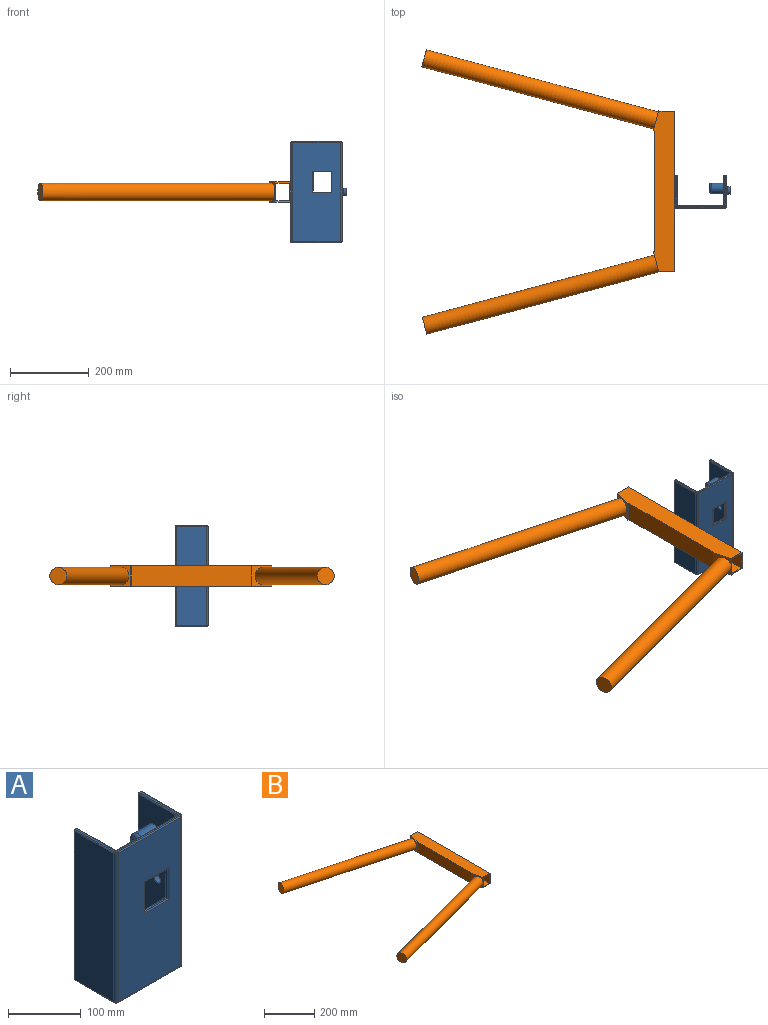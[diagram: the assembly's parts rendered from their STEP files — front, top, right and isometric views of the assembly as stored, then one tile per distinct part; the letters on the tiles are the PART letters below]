
ASSEMBLY  parts=2 mates=1
PART A: 63 faces, bbox 141.6x83.2x254.2 mm
  f0: cylinder r=5.08mm len=243.28mm, axis (0,0,-1), area 1941.3mm2, adj f1,f11,f12,f56
  f1: bspline ~5.34x5.34mm, area 34.1mm2, adj f0,f4,f11,f12,f37,f39
  f2: cylinder r=5.08mm len=243.28mm, axis (0,0,1), area 1941.3mm2, adj f3,f11,f17,f55
  f3: bspline ~5.34x5.34mm, area 34.1mm2, adj f2,f7,f11,f17,f34,f36
  f4: bspline ~5.77x5.77mm, area 13.8mm2, adj f1,f37,f39
  f5: bspline ~5.62x5.59mm, area 13.9mm2, adj f36,f38,f56
  f6: bspline ~5.77x5.77mm, area 13.8mm2, adj f35,f37,f55
  f7: bspline ~5.62x5.59mm, area 13.9mm2, adj f3,f34,f36
  f8: plane 128.27x80.96mm, normal (0,0,1), area 896mm2, adj f13,f16,f34,f36,f38,f42,f44,f46
  f9: plane 128.27x80.96mm, normal (0,0,-1), area 896mm2, adj f13,f16,f35,f37,f39,f43,f45,f47
  f10: plane 250.83x121.29mm, normal (0,-1,0), area 27782.2mm2, adj f29,f30,f31,f32,f44,f45,f50,f53
  f11: plane 251.07x108.83mm, normal (0,1,0), area 24682.4mm2, adj f0,f1,f2,f3,f25,f26,f27,f28
  f12: plane 251.07x69.78mm, normal (1,0,0), area 17440.5mm2, adj f0,f1,f38,f39,f40,f56
  f13: plane 254x3.18mm, normal (0,1,0), area 806.4mm2, adj f8,f9,f40,f48
  f14: plane 250.83x75.88mm, normal (-1,0,0), area 19033.2mm2, adj f46,f47,f48,f53
  f15: plane 250.83x75.88mm, normal (1,0,0), area 18526.5mm2, adj f41,f42,f43,f50,f62
  f16: plane 254x3.18mm, normal (0,1,0), area 806.4mm2, adj f8,f9,f33,f41
  f17: plane 251.07x69.78mm, normal (-1,0,0), area 16300.4mm2, adj f2,f3,f18,f20,f33,f34,f35,f55
  f18: cylinder r=12.7mm len=31.75mm, axis (1,0,0), area 2533.5mm2, adj f17,f58
  f19: plane 15.24x15.24mm, normal (-1,0,0), area 182.4mm2, adj f58
  f20: cylinder r=12.7mm len=31.75mm, axis (1,0,0), area 2533.5mm2, adj f17,f57
  f21: plane 15.24x15.24mm, normal (-1,0,0), area 182.4mm2, adj f57
  f22: plane 45.72x3.18mm, normal (0,0,-1), area 145.2mm2, adj f23,f25,f28,f29
  f23: plane 50.8x3.18mm, normal (1,0,0), area 161.3mm2, adj f22,f24,f27,f30
  f24: plane 45.72x3.18mm, normal (0,0,1), area 145.2mm2, adj f23,f25,f26,f32
  f25: plane 53.98x4.76mm, normal (-1,0,0), area 243mm2, adj f11,f22,f24,f26,f28,f31
  f26: cylinder r=1.59mm len=47.31mm, axis (1,0,0), area 116mm2, adj f11,f24,f25,f27
  f27: cylinder r=1.59mm len=53.98mm, axis (0,0,-1), area 130.6mm2, adj f11,f23,f26,f28
  f28: cylinder r=1.59mm len=47.31mm, axis (-1,0,0), area 116mm2, adj f11,f22,f25,f27
  f29: cylinder r=1.59mm len=48.9mm, axis (1,0,0), area 118mm2, adj f10,f22,f30,f31
  f30: cylinder r=1.59mm len=53.98mm, axis (0,0,1), area 130.6mm2, adj f10,f23,f29,f32
  f31: cylinder r=1.59mm len=53.98mm, axis (0,0,-1), area 130.6mm2, adj f10,f25,f29,f32
  f32: cylinder r=1.59mm len=48.9mm, axis (-1,0,0), area 118mm2, adj f10,f24,f30,f31
  f33: cylinder r=1.59mm len=254mm, axis (0,0,1), area 629.4mm2, adj f16,f17,f34,f35
  f34: cylinder r=1.59mm len=77.79mm, axis (0,1,0), area 182mm2, adj f3,f7,f8,f17,f33
  f35: cylinder r=1.59mm len=77.79mm, axis (0,-1,0), area 182mm2, adj f6,f9,f17,f33,f55
  f36: cylinder r=1.59mm len=121.92mm, axis (1,0,0), area 284mm2, adj f3,f5,f7,f8,f11,f56
  f37: cylinder r=1.59mm len=121.92mm, axis (-1,0,0), area 284mm2, adj f1,f4,f6,f9,f11,f55
  f38: cylinder r=1.59mm len=77.79mm, axis (0,-1,0), area 182mm2, adj f5,f8,f12,f40,f56
  f39: cylinder r=1.59mm len=77.79mm, axis (0,1,0), area 182mm2, adj f1,f4,f9,f12,f40
  f40: cylinder r=1.59mm len=254mm, axis (0,0,1), area 629.4mm2, adj f12,f13,f38,f39
  f41: cylinder r=1.59mm len=254mm, axis (0,0,-1), area 629.4mm2, adj f15,f16,f42,f43
  f42: cylinder r=1.59mm len=77.47mm, axis (0,-1,0), area 191.2mm2, adj f8,f15,f41,f49
  f43: cylinder r=1.59mm len=77.47mm, axis (0,1,0), area 191.2mm2, adj f9,f15,f41,f51
  f44: cylinder r=1.59mm len=121.29mm, axis (-1,0,0), area 302.4mm2, adj f8,f10,f49,f52
  f45: cylinder r=1.59mm len=121.29mm, axis (1,0,0), area 302.4mm2, adj f9,f10,f51,f54
  f46: cylinder r=1.59mm len=77.47mm, axis (0,1,0), area 191.2mm2, adj f8,f14,f48,f52
  f47: cylinder r=1.59mm len=77.47mm, axis (0,-1,0), area 191.2mm2, adj f9,f14,f48,f54
  f48: cylinder r=1.59mm len=254mm, axis (0,0,-1), area 629.4mm2, adj f13,f14,f46,f47
  f49: torus R=3.49mm, axis (0,0,1), area 17.6mm2, adj f8,f42,f44,f50
  f50: cylinder r=5.08mm len=250.83mm, axis (0,0,-1), area 2001.5mm2, adj f10,f15,f49,f51
  f51: torus R=3.49mm, axis (0,0,1), area 17.6mm2, adj f9,f43,f45,f50
  f52: torus R=3.49mm, axis (0,0,1), area 17.6mm2, adj f8,f44,f46,f53
  f53: cylinder r=5.08mm len=250.83mm, axis (0,0,1), area 2001.5mm2, adj f10,f14,f52,f54
  f54: torus R=3.49mm, axis (0,0,1), area 17.6mm2, adj f9,f45,f47,f53
  f55: bspline ~5.34x5.34mm, area 34.1mm2, adj f2,f6,f11,f17,f35,f37
  f56: bspline ~5.34x5.34mm, area 34.1mm2, adj f0,f5,f11,f12,f36,f38
  f57: torus R=7.62mm, axis (1,0,0), area 544.2mm2, adj f20,f21
  f58: torus R=7.62mm, axis (1,0,0), area 544.2mm2, adj f18,f19
  f59: cylinder r=9.53mm len=19.05mm, axis (-1,0,0), area 380mm2, adj f60,f62
  f60: plane 19.05x19.05mm, normal (1,0,0), area 158.3mm2, adj f59,f61
  f61: cylinder r=6.35mm len=15.88mm, axis (1,0,0), area 633.4mm2, adj f17,f60
  f62: cone r=9.53mm half-angle=45deg, axis (-1,0,0), area 313.5mm2, adj f15,f59
PART B: 23 faces, bbox 641.4x721.7x50.8 mm
  f0: plane 408.04x53.87mm, normal (0,0,1), area 20283.3mm2, adj f5,f7,f8,f9,f11,f12,f13,f17
  f1: plane 408.04x53.87mm, normal (0,0,-1), area 20283.3mm2, adj f5,f7,f8,f9,f11,f12,f13,f17
  f2: plane 406.4x44.45mm, normal (0,0,-1), area 17653.6mm2, adj f4,f6,f8,f9,f10,f16
  f3: plane 406.4x44.45mm, normal (0,0,1), area 17653.6mm2, adj f4,f6,f8,f9,f10,f16
  f4: plane 328.08x44.45mm, normal (1,0,0), area 14583.3mm2, adj f2,f3,f10,f16
  f5: plane 304.39x50.8mm, normal (-1,0,0), area 15462.8mm2, adj f0,f1,f12,f17
  f6: plane 406.4x44.45mm, normal (-1,0,0), area 18064.5mm2, adj f2,f3,f8,f9
  f7: plane 406.4x50.8mm, normal (1,0,0), area 20645.1mm2, adj f0,f1,f8,f9
  f8: plane 50.8x37.13mm, normal (0,-1,0), area 376.9mm2, adj f0,f1,f2,f3,f6,f7,f18
  f9: plane 50.8x37.13mm, normal (0,1,0), area 376.9mm2, adj f0,f1,f2,f3,f6,f7,f11
  f10: plane 44.45x39.16mm, normal (0.97,-0.26,0), area 1802mm2, adj f2,f3,f4,f11
  f11: plane 50.8x3.07mm, normal (0.26,0.97,0), area 161.3mm2, adj f0,f1,f9,f10,f13
  f12: plane 50.8x3.07mm, normal (-0.26,-0.97,0), area 161.3mm2, adj f0,f1,f5,f13
  f13: plane 51.01x50.8mm, normal (-0.97,0.26,0), area 1130.8mm2, adj f0,f1,f11,f12,f14
  f14: cylinder r=22.23mm len=600.33mm, axis (0.97,-0.26,0), area 85126.9mm2, adj f13,f15
  f15: plane 44.45x42.94mm, normal (-0.97,0.26,0), area 1551.8mm2, adj f14
  f16: plane 44.45x39.16mm, normal (0.97,0.26,0), area 1802mm2, adj f2,f3,f4,f18
  f17: plane 50.8x3.07mm, normal (-0.26,0.97,0), area 161.3mm2, adj f0,f1,f5,f19
  f18: plane 50.8x3.07mm, normal (0.26,-0.97,0), area 161.3mm2, adj f0,f1,f8,f16,f19,f20
  f19: plane 51.01x50.8mm, normal (-0.97,-0.26,0), area 1142.1mm2, adj f0,f1,f17,f18,f21
  f20: plane 14.29x1.14mm, normal (0.97,0.26,0), area 11.3mm2, adj f18,f21
  f21: cylinder r=22.23mm len=600.33mm, axis (0.97,0.26,0), area 85126.9mm2, adj f19,f20,f22
  f22: plane 44.45x42.94mm, normal (-0.97,-0.26,0), area 1551.8mm2, adj f21
PLACE A t=(149.57,-105.37,-182.62)mm
PLACE B t=(58.45,-106.8,-182.62)mm
MATE fastened A.f14 <-> B.f7  axis (-1,0,0) through (83.85,-106.8,-182.62)mm
